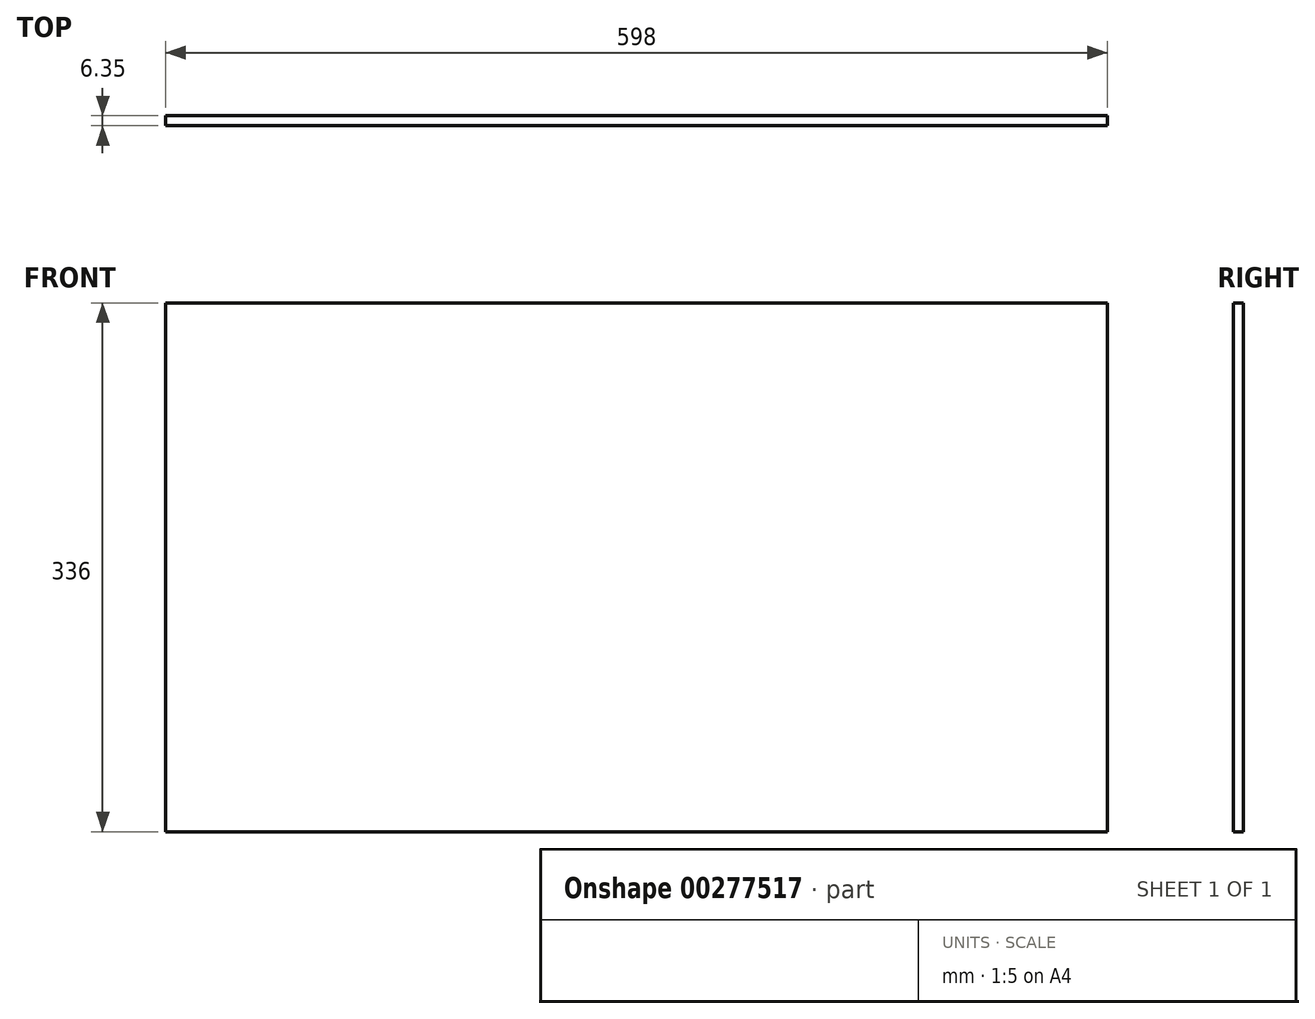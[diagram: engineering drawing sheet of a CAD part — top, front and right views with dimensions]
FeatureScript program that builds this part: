
annotation { "Feature Type Name" : "Feature", "Feature Type Description" : "" }
export const myFeature = defineFeature(function(context is Context, id is Id, definition is map)
    precondition{}
    {
        {
            var Q0;
            Q0=qCreatedBy(makeId("Front.planeOp"),FACE);
            var sketch = newSketch(context, id + "F0", { "sketchPlane" : qUnion([Q0])});
            skLineSegment(sketch, "E0.bottom", {"start": v(-299, 168) * mm, "end": v(299, 168) * mm});
            skLineSegment(sketch, "E0.top", {"start": v(-299, -168) * mm, "end": v(299, -168) * mm});
            skLineSegment(sketch, "E0.left", {"start": v(-299, 168) * mm, "end": v(-299, -168) * mm});
            skLineSegment(sketch, "E0.right", {"start": v(299, 168) * mm, "end": v(299, -168) * mm});
            skPoint(sketch, "E0.middle", {"position": v(0, 0) * mm});
            skSolve(sketch);
        }
        {
            var Q0;
            Q0=makeQuery(id+"F0.imprint","IMPRINT",FACE,{"disambiguationData":[TD([[makeQuery(id+"F0.imprint","IMPRINT",EDGE,{"derivedFrom":sQuery(id+"F0.wireOp",EDGE,"E0.bottom")}),-1.0]])]});
            extrude(context, id + "F1", {"entities" : qUnion([Q0]), "depth" : 6.35 * mm});
        }
    });
